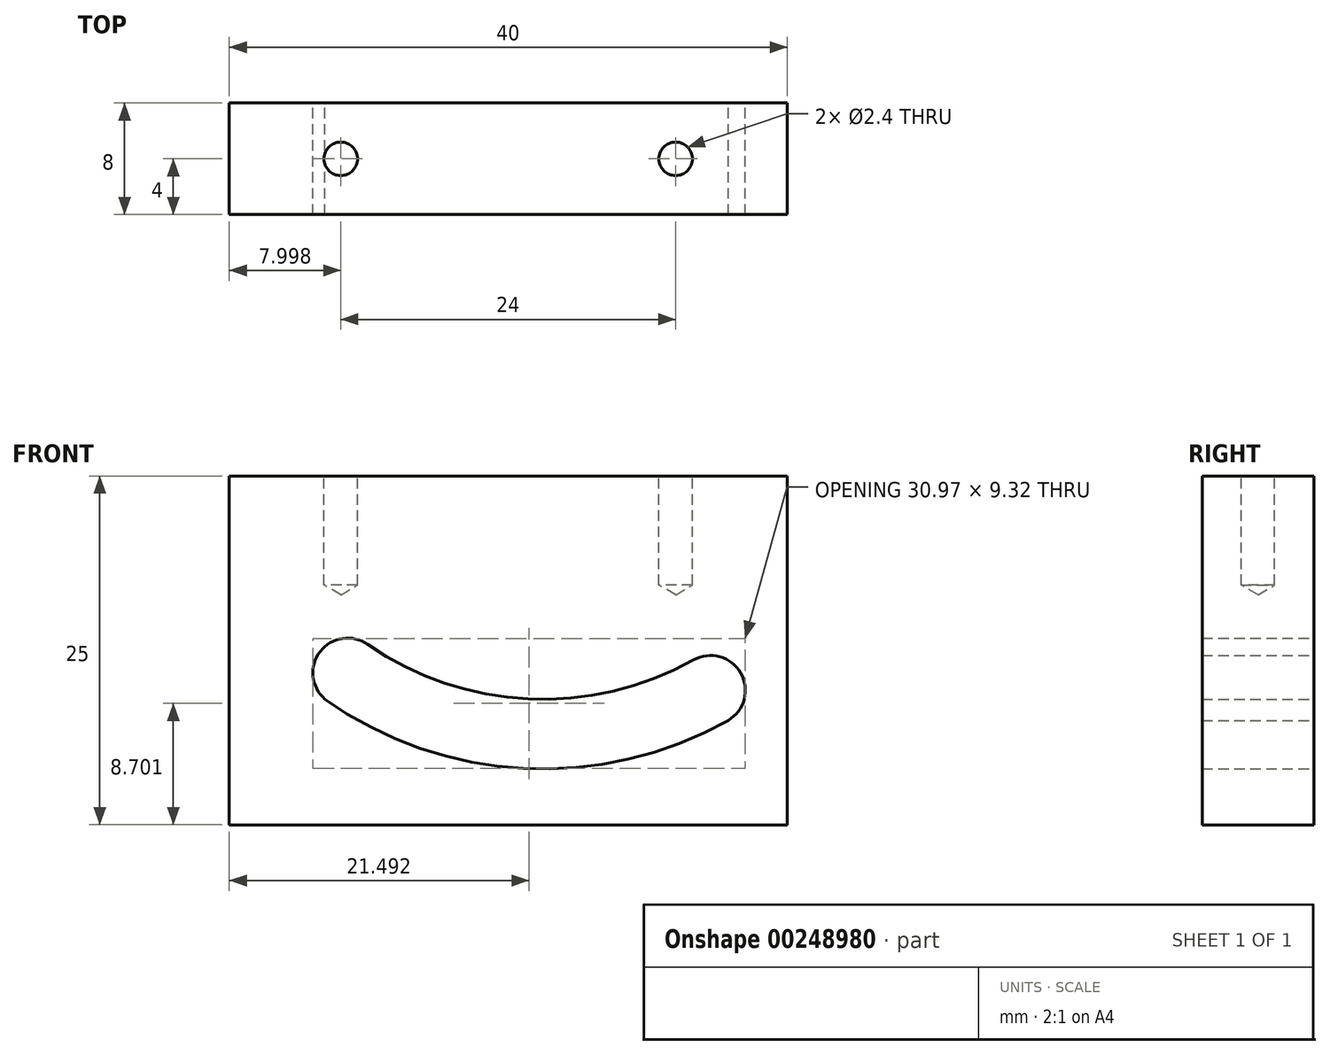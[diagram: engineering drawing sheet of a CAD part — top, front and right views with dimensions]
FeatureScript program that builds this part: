
annotation { "Feature Type Name" : "Feature", "Feature Type Description" : "" }
export const myFeature = defineFeature(function(context is Context, id is Id, definition is map)
    precondition{}
    {
        {
            var Q0;
            Q0=qCreatedBy(makeId("Front.planeOp"),FACE);
            var sketch = newSketch(context, id + "F0", { "sketchPlane" : qUnion([Q0])});
            skLineSegment(sketch, "E0.bottom", {"start": v(17.94, 14.1) * mm, "end": v(-22.06, 14.1) * mm});
            skLineSegment(sketch, "E0.top", {"start": v(17.94, -10.9) * mm, "end": v(-22.06, -10.9) * mm});
            skLineSegment(sketch, "E0.left", {"start": v(17.94, 14.1) * mm, "end": v(17.94, -10.9) * mm});
            skLineSegment(sketch, "E0.right", {"start": v(-22.06, 14.1) * mm, "end": v(-22.06, -10.9) * mm});
            skPoint(sketch, "E0.middle", {"position": v(0, 0) * mm});
            skPoint(sketch, "E1", {"position": v(0.44, 20.1) * mm});
            skArc(sketch, "E2", {"start": v(15.66, 0.91) * mm, "mid": v(14.1, -0.24) * mm, "end": v(12.44, -1.25) * mm, "construction": true});
            skArc(sketch, "E3.0", {"start": v(11.21, 0.93) * mm, "mid": v(-0.62, -1.87) * mm, "end": v(-12.13, 2.05) * mm});
            skArc(sketch, "E4", {"start": v(13.7, -3.4) * mm, "mid": v(14.6, 0) * mm, "end": v(11.21, 0.93) * mm});
            skArc(sketch, "E5", {"start": v(-12.13, 2.05) * mm, "mid": v(-15.53, 1.54) * mm, "end": v(-15.2, -1.89) * mm});
            skArc(sketch, "E6.trimOffspring", {"start": v(12.44, -1.25) * mm, "mid": v(-6.46, -3.4) * mm, "end": v(-21.2, 8.62) * mm, "construction": true});
            skArc(sketch, "E7.trimOffspring", {"start": v(13.7, -3.4) * mm, "mid": v(-0.97, -6.85) * mm, "end": v(-15.2, -1.89) * mm});
            skSolve(sketch);
        }
        {
            var Q0;
            Q0=makeQuery(id+"F0.imprint","IMPRINT",FACE,{"disambiguationData":[TD([[makeQuery(id+"F0.imprint","IMPRINT",EDGE,{"derivedFrom":sQuery(id+"F0.wireOp",EDGE,"E0.bottom")}),1.0]])]});
            extrude(context, id + "F1", {"entities" : qUnion([Q0]), "endBound" : BoundingType.SYMMETRIC, "depth" : 8 * mm});
        }
        {
            var Q0;
            Q0=makeQuery(id+"F1.opExtrude","SWEPT_FACE",FACE,{"disambiguationData":[OSD([sQuery(id+"F0.wireOp",EDGE,"E0.bottom")])]});
            var sketch = newSketch(context, id + "F2", { "sketchPlane" : qUnion([Q0])});
            skPoint(sketch, "E8", {"position": v(9.94, 0) * mm});
            skPoint(sketch, "E9", {"position": v(-14.06, 0) * mm});
            skSolve(sketch);
        }
        {
            var Q0;
            Q0=sQuery(id+"F2.wireOp",VERTEX,"E9");
            var Q1;
            Q1=sQuery(id+"F2.wireOp",VERTEX,"E8");
            var Q2;
            Q2=makeQuery(id+"F1.opExtrude","SWEPT_BODY",BODY,{"disambiguationData":[OSD([sQuery(id+"F0.wireOp",EDGE,"E0.bottom"),sQuery(id+"F0.wireOp",EDGE,"E0.top"),sQuery(id+"F0.wireOp",EDGE,"E0.left"),sQuery(id+"F0.wireOp",EDGE,"E0.right"),sQuery(id+"F0.wireOp",EDGE,"E3.0"),sQuery(id+"F0.wireOp",EDGE,"E4"),sQuery(id+"F0.wireOp",EDGE,"E5"),sQuery(id+"F0.wireOp",EDGE,"E7.trimOffspring")])]});
            hole(context, id + "F3", {"style" : HoleStyle.SIMPLE, "endStyle" : HoleEndStyle.BLIND, "standardTappedOrClearance" : lookupTablePath({ "standard" : "ISO", "engagement" : "75%", "pitch" : "0.6 mm", "size" : "M3", "type" : "Tapped" }), "standardBlindInLast" : lookupTablePath({ "standard" : "ISO", "engagement" : "75%", "pitch" : "0.6 mm", "size" : "M3", "type" : "Tapped" }), "holeDiameter" : 2.4 * mm, "showTappedDepth" : true, "holeDepth" : 7.8 * mm, "tappedDepth" : 6 * mm, "tapClearance" : 3, "startFromSketch" : true, "locations" : qUnion([Q0, Q1]), "scope" : qUnion([Q2])});
        }
    });
